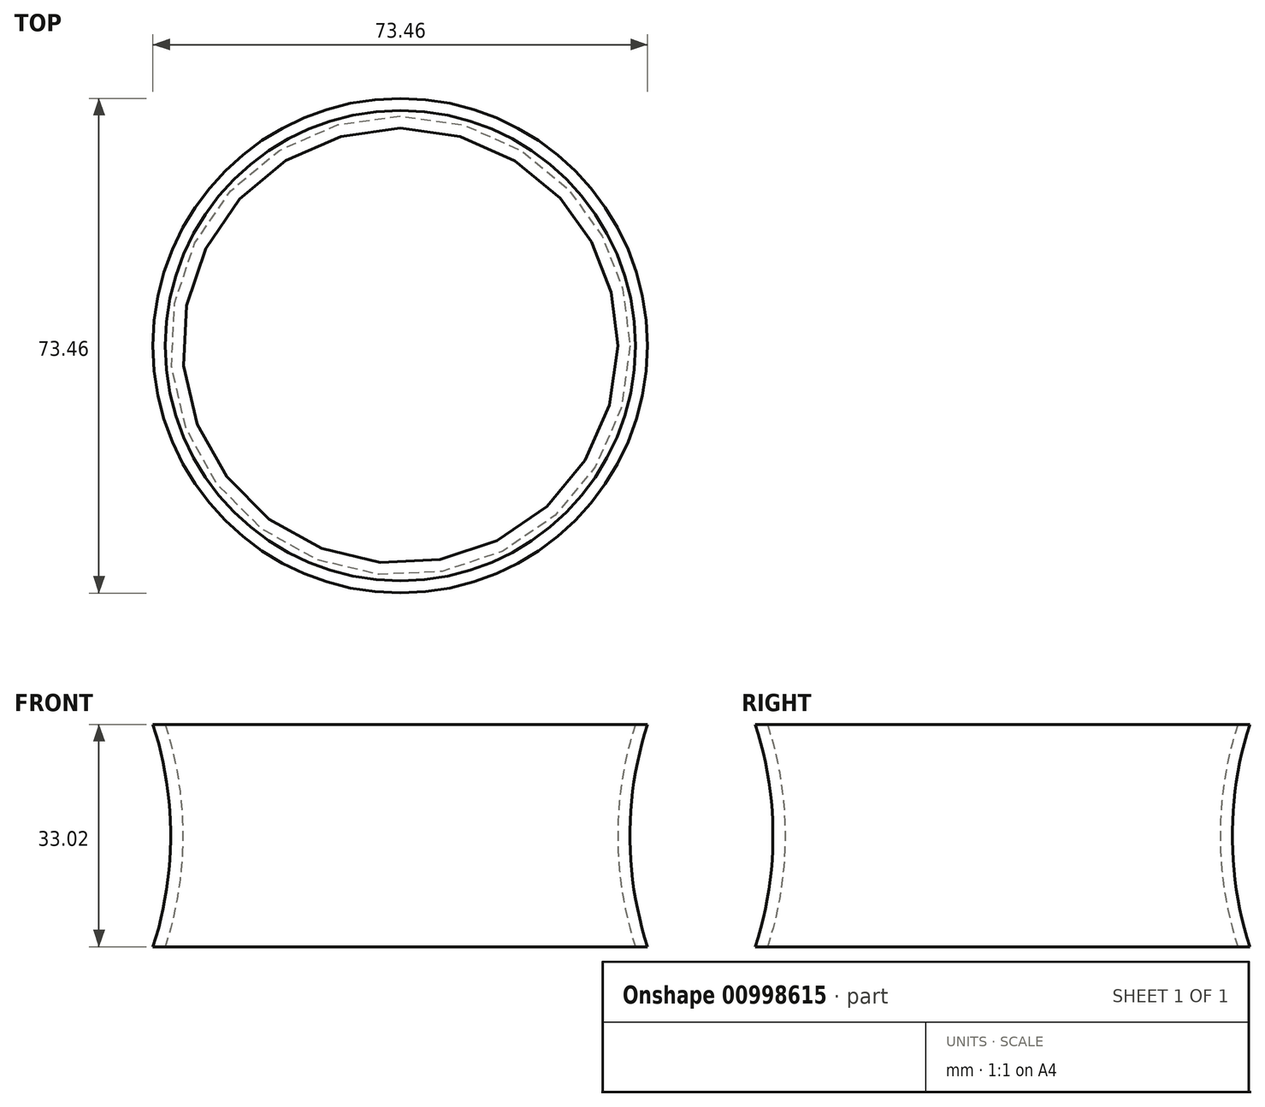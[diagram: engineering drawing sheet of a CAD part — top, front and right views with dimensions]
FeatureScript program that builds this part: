
annotation { "Feature Type Name" : "Feature", "Feature Type Description" : "" }
export const myFeature = defineFeature(function(context is Context, id is Id, definition is map)
    precondition{}
    {
        {
            var Q0;
            Q0=qCreatedBy(makeId("Front.planeOp"),FACE);
            var sketch = newSketch(context, id + "F0", { "sketchPlane" : qUnion([Q0])});
            skLineSegment(sketch, "E0", {"start": v(0, 61.21) * mm, "end": v(0, -86.97) * mm, "construction": true});
            skPoint(sketch, "E1", {"position": v(-34.93, 0) * mm});
            skPoint(sketch, "E2", {"position": v(-85.73, 0) * mm});
            skPoint(sketch, "E3", {"position": v(-34.92, 16.51) * mm});
            skPoint(sketch, "E4", {"position": v(-34.92, -16.51) * mm});
            skArc(sketch, "E5", {"start": v(-34.93, 16.5) * mm, "mid": v(-32.3, 0) * mm, "end": v(-34.93, -16.51) * mm});
            skPoint(sketch, "E6", {"position": v(-87.53, 0) * mm});
            skPoint(sketch, "E7", {"position": v(-36.72, 16.51) * mm});
            skPoint(sketch, "E8", {"position": v(-36.73, -16.51) * mm});
            skArc(sketch, "E9", {"start": v(-36.73, 16.5) * mm, "mid": v(-34.1, 0) * mm, "end": v(-36.73, -16.51) * mm});
            skLineSegment(sketch, "E10", {"start": v(-36.72, 16.51) * mm, "end": v(-34.92, 16.51) * mm});
            skLineSegment(sketch, "E11", {"start": v(-36.73, -16.51) * mm, "end": v(-34.92, -16.51) * mm});
            skSolve(sketch);
        }
        {
            var Q0;
            Q0=qSketchRegion(id+"F0",true);
            var Q1;
            Q1=sQuery(id+"F0.wireOp",EDGE,"E0");
            revolve(context, id + "F1", {"surfaceOperationType" : NewSurfaceOperationType.NEW, "entities" : qUnion([Q0]), "axis" : qUnion([Q1]), "revolveType" : RevolveType.FULL});
        }
    });
